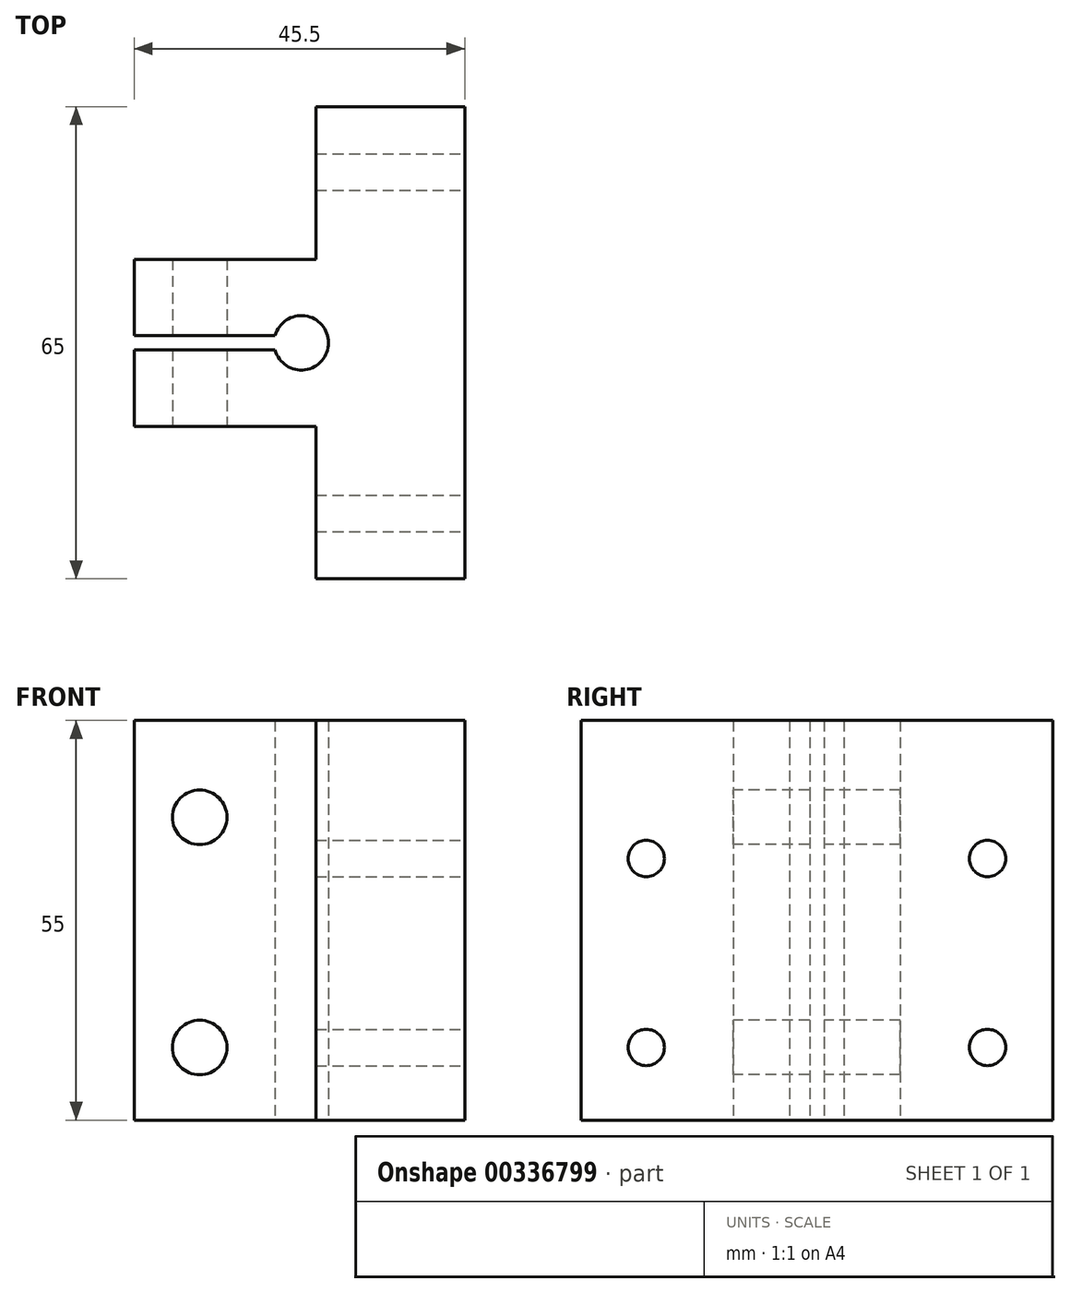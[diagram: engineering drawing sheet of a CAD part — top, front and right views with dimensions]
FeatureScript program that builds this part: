
annotation { "Feature Type Name" : "Feature", "Feature Type Description" : "" }
export const myFeature = defineFeature(function(context is Context, id is Id, definition is map)
    precondition{}
    {
        {
            var Q0;
            Q0=qCreatedBy(makeId("Top.planeOp"),FACE);
            var sketch = newSketch(context, id + "F0", { "sketchPlane" : qUnion([Q0])});
            skLineSegment(sketch, "E0", {"start": v(63.35, 38.28) * mm, "end": v(63.35, -26.72) * mm});
            skLineSegment(sketch, "E1", {"start": v(63.35, 38.28) * mm, "end": v(42.85, 38.28) * mm});
            skLineSegment(sketch, "E2", {"start": v(63.35, -26.72) * mm, "end": v(42.85, -26.72) * mm});
            skLineSegment(sketch, "E3", {"start": v(42.85, 38.28) * mm, "end": v(42.85, 17.28) * mm});
            skLineSegment(sketch, "E4", {"start": v(42.85, -26.72) * mm, "end": v(42.85, -5.72) * mm});
            skLineSegment(sketch, "E5", {"start": v(42.85, 17.28) * mm, "end": v(17.85, 17.28) * mm});
            skLineSegment(sketch, "E6", {"start": v(42.85, -5.72) * mm, "end": v(17.85, -5.72) * mm});
            skLineSegment(sketch, "E7", {"start": v(17.85, 6.78) * mm, "end": v(17.85, 17.28) * mm});
            skLineSegment(sketch, "E8", {"start": v(17.85, 4.78) * mm, "end": v(17.85, -5.72) * mm});
            skArc(sketch, "E9", {"start": v(37.24, 4.78) * mm, "mid": v(44.6, 5.78) * mm, "end": v(37.24, 6.78) * mm});
            skPoint(sketch, "E10.end.orphan", {"position": v(63.35, 5.78) * mm});
            skLineSegment(sketch, "E11", {"start": v(17.85, 6.78) * mm, "end": v(37.24, 6.78) * mm});
            skLineSegment(sketch, "E12", {"start": v(17.85, 4.78) * mm, "end": v(37.24, 4.78) * mm});
            skSolve(sketch);
        }
        {
            var Q0;
            Q0 = qSketchRegion(id + "F0", true);
            extrude(context, id + "F1", {"entities" : qUnion([Q0]), "depth" : 55 * mm});
        }
        {
            var Q0;
            Q0=makeQuery(id+"F1.opExtrude","SWEPT_FACE",FACE,{"disambiguationData":[OSD([sQuery(id+"F0.wireOp",EDGE,"E0")])]});
            var sketch = newSketch(context, id + "F2", { "sketchPlane" : qUnion([Q0])});
            skCircle(sketch, "E13", {"center": v(-17.72, 36) * mm, "radius": 2.5 * mm});
            skCircle(sketch, "E14", {"center": v(-17.72, 10) * mm, "radius": 2.5 * mm});
            skCircle(sketch, "E15", {"center": v(29.28, 36) * mm, "radius": 2.5 * mm});
            skCircle(sketch, "E16", {"center": v(29.28, 10) * mm, "radius": 2.5 * mm});
            skPoint(sketch, "E17.orphan", {"position": v(-17.72, -11.57) * mm});
            skPoint(sketch, "E18.end.orphan", {"position": v(38.28, -11.57) * mm});
            skSolve(sketch);
        }
        {
            var Q0;
            Q0=makeQuery(id+"F2.imprint","IMPRINT",FACE,{"disambiguationData":[TD([[makeQuery(id+"F2.imprint","IMPRINT",EDGE,{"derivedFrom":sQuery(id+"F2.wireOp",EDGE,"E16")}),1.0]])]});
            var Q1;
            Q1=makeQuery(id+"F2.imprint","IMPRINT",FACE,{"disambiguationData":[TD([[makeQuery(id+"F2.imprint","IMPRINT",EDGE,{"derivedFrom":sQuery(id+"F2.wireOp",EDGE,"E15")}),1.0]])]});
            var Q2;
            Q2=makeQuery(id+"F2.imprint","IMPRINT",FACE,{"disambiguationData":[TD([[makeQuery(id+"F2.imprint","IMPRINT",EDGE,{"derivedFrom":sQuery(id+"F2.wireOp",EDGE,"E14")}),1.0]])]});
            var Q3;
            Q3=makeQuery(id+"F2.imprint","IMPRINT",FACE,{"disambiguationData":[TD([[makeQuery(id+"F2.imprint","IMPRINT",EDGE,{"derivedFrom":sQuery(id+"F2.wireOp",EDGE,"E13")}),1.0]])]});
            extrude(context, id + "F3", {"entities" : qUnion([Q0, Q1, Q2, Q3]), "operationType" : NewBodyOperationType.REMOVE, "endBound" : BoundingType.THROUGH_ALL, "oppositeDirection" : true, "depth" : 25 * mm});
        }
        {
            var Q0;
            Q0=makeQuery(id+"F1.opExtrude","SWEPT_FACE",FACE,{"disambiguationData":[OSD([sQuery(id+"F0.wireOp",EDGE,"E6")])]});
            var sketch = newSketch(context, id + "F4", { "sketchPlane" : qUnion([Q0])});
            skCircle(sketch, "E19", {"center": v(26.85, 41.68) * mm, "radius": 3.75 * mm});
            skCircle(sketch, "E20", {"center": v(26.85, 10) * mm, "radius": 3.75 * mm});
            skPoint(sketch, "E21.start.orphan", {"position": v(10, 41.68) * mm});
            skPoint(sketch, "E22.start.orphan", {"position": v(10, 0) * mm});
            skSolve(sketch);
        }
        {
            var Q0;
            Q0=makeQuery(id+"F4.imprint","IMPRINT",FACE,{"disambiguationData":[TD([[makeQuery(id+"F4.imprint","IMPRINT",EDGE,{"derivedFrom":sQuery(id+"F4.wireOp",EDGE,"E19")}),1.0]])]});
            var Q1;
            Q1=makeQuery(id+"F4.imprint","IMPRINT",FACE,{"disambiguationData":[TD([[makeQuery(id+"F4.imprint","IMPRINT",EDGE,{"derivedFrom":sQuery(id+"F4.wireOp",EDGE,"E20")}),1.0]])]});
            extrude(context, id + "F5", {"entities" : qUnion([Q0, Q1]), "operationType" : NewBodyOperationType.REMOVE, "endBound" : BoundingType.THROUGH_ALL, "oppositeDirection" : true, "depth" : 25 * mm});
        }
    });
